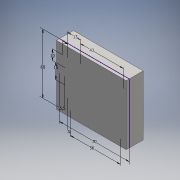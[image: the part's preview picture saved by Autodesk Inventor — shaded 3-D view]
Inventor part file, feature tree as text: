
AUTODESK INVENTOR PART (.ipt)
format: ipt  version: 2016 (Build 200138000, 138)  size: 119,808 bytes
history: native  units: mm
features: extrude x2, sketch x1
ambient origin geometry x8: Origin, YZ Plane, XZ Plane, XY Plane, X Axis, Y Axis, Z Axis, Center Point
bodies: Solid1 (feature_tree)
feature tree (3):
  sketch  "Sketch1"  dims[d0=70.0mm d1=60.0mm d2=5.5mm d3=15.0mm d5=10.0mm d6=5.0mm d11=50.0mm d12=3.0mm d13=43.0mm d14=13.0mm d15=14.0mm d16=0.0mm d17=3.0mm d18=0.0mm]
  extrude  "Extrusion1"  Depth=60.0mm
  extrude  "Extrusion2"  Depth=3.0mm
